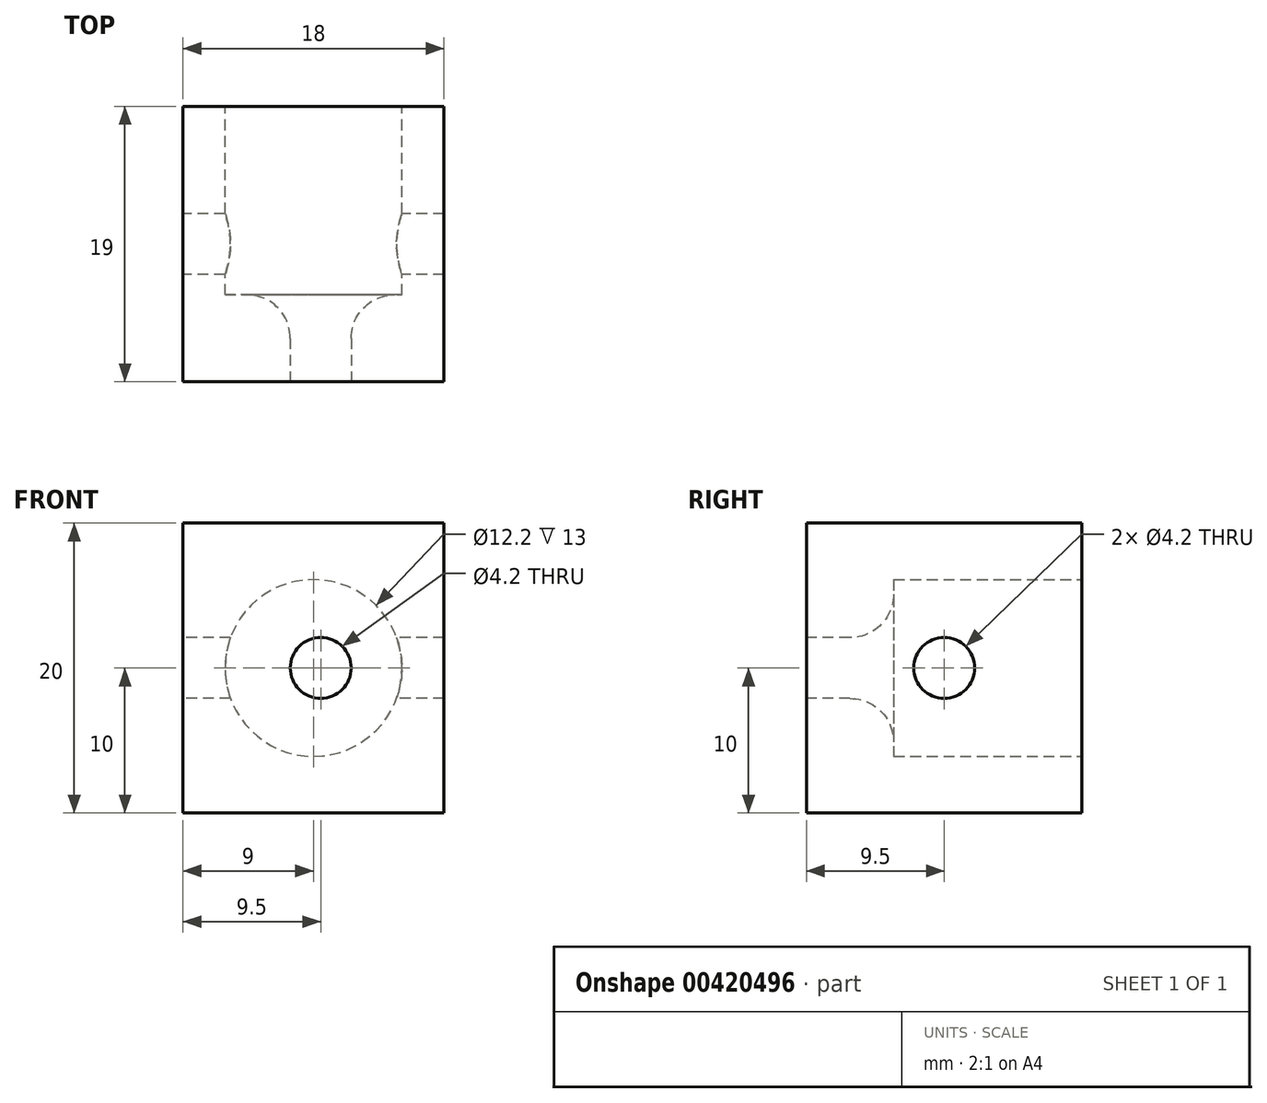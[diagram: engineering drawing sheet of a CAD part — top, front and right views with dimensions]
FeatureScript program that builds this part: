
annotation { "Feature Type Name" : "Feature", "Feature Type Description" : "" }
export const myFeature = defineFeature(function(context is Context, id is Id, definition is map)
    precondition{}
    {
        {
            var Q0;
            Q0=qCreatedBy(makeId("Top.planeOp"),FACE);
            var sketch = newSketch(context, id + "F0", { "sketchPlane" : qUnion([Q0])});
            skLineSegment(sketch, "E0.bottom", {"start": v(9, -9.5) * mm, "end": v(-9, -9.5) * mm});
            skLineSegment(sketch, "E0.top", {"start": v(9, 9.5) * mm, "end": v(-9, 9.5) * mm});
            skLineSegment(sketch, "E0.left", {"start": v(9, -9.5) * mm, "end": v(9, 9.5) * mm});
            skLineSegment(sketch, "E0.right", {"start": v(-9, -9.5) * mm, "end": v(-9, 9.5) * mm});
            skPoint(sketch, "E0.middle", {"position": v(0, 0) * mm});
            skSolve(sketch);
        }
        {
            var Q0;
            Q0=makeQuery(id+"F0.imprint","IMPRINT",FACE,{"disambiguationData":[TD([[makeQuery(id+"F0.imprint","IMPRINT",EDGE,{"derivedFrom":sQuery(id+"F0.wireOp",EDGE,"E0.bottom")}),-1.0]])]});
            extrude(context, id + "F1", {"entities" : qUnion([Q0]), "depth" : 20 * mm});
        }
        {
            var Q0;
            Q0=makeQuery(id+"F1.opExtrude","SWEPT_FACE",FACE,{"disambiguationData":[OSD([sQuery(id+"F0.wireOp",EDGE,"E0.bottom")])]});
            var sketch = newSketch(context, id + "F2", { "sketchPlane" : qUnion([Q0])});
            skLineSegment(sketch, "E1", {"start": v(-9, 10) * mm, "end": v(9, 10) * mm, "construction": true});
            skCircle(sketch, "E2", {"center": v(0.5, 10) * mm, "radius": 2.1 * mm});
            skSolve(sketch);
        }
        {
            var Q0;
            Q0=makeQuery(id+"F1.opExtrude","SWEPT_FACE",FACE,{"disambiguationData":[OSD([sQuery(id+"F0.wireOp",EDGE,"E0.top")])]});
            var sketch = newSketch(context, id + "F3", { "sketchPlane" : qUnion([Q0])});
            skLineSegment(sketch, "E3", {"start": v(-9, 10) * mm, "end": v(9, 10) * mm, "construction": true});
            skCircle(sketch, "E4", {"center": v(0, 10) * mm, "radius": 6.1 * mm});
            skSolve(sketch);
        }
        {
            var Q0;
            Q0=makeQuery(id+"F3.imprint","IMPRINT",FACE,{"disambiguationData":[TD([[makeQuery(id+"F3.imprint","IMPRINT",EDGE,{"derivedFrom":sQuery(id+"F3.wireOp",EDGE,"E4")}),1.0]])]});
            extrude(context, id + "F4", {"entities" : qUnion([Q0]), "operationType" : NewBodyOperationType.REMOVE, "oppositeDirection" : true, "depth" : 13 * mm});
        }
        {
            var Q0;
            Q0=makeQuery(id+"F2.imprint","IMPRINT",FACE,{"disambiguationData":[TD([[makeQuery(id+"F2.imprint","IMPRINT",EDGE,{"derivedFrom":sQuery(id+"F2.wireOp",EDGE,"E2")}),1.0]])]});
            extrude(context, id + "F5", {"entities" : qUnion([Q0]), "operationType" : NewBodyOperationType.REMOVE, "oppositeDirection" : true, "depth" : 18 * mm});
        }
        {
            var Q0;
            Q0=makeQuery(id+"F5.boolean.opBoolean","INTERSECT",EDGE,{"derivedFrom":[makeQuery(id+"F4.boolean.opBoolean","COPY",FACE,{"derivedFrom":makeQuery(id+"F4.opExtrude","CAP_FACE",FACE,{"disambiguationData":[OSD([sQuery(id+"F3.wireOp",EDGE,"E4")])],"isStart":false})}),makeQuery(id+"F5.opExtrude","SWEPT_FACE",FACE,{"disambiguationData":[OSD([sQuery(id+"F2.wireOp",EDGE,"E2")])]})]});
            fillet(context, id + "F6", {"entities" : qUnion([Q0]), "radius" : 3 * mm, "tangentPropagation" : true, "allowEdgeOverflow" : false});
        }
        {
            var Q0;
            Q0=makeQuery(id+"F1.opExtrude","SWEPT_FACE",FACE,{"disambiguationData":[OSD([sQuery(id+"F0.wireOp",EDGE,"E0.right")])]});
            var sketch = newSketch(context, id + "F7", { "sketchPlane" : qUnion([Q0])});
            skLineSegment(sketch, "E5", {"start": v(-9.5, 10) * mm, "end": v(9.5, 10) * mm, "construction": true});
            skCircle(sketch, "E6", {"center": v(0, 10) * mm, "radius": 2.1 * mm});
            skLineSegment(sketch, "E7", {"start": v(-9.5, 10) * mm, "end": v(9.5, 10) * mm});
            skSolve(sketch);
        }
        {
            var Q0;
            Q0=makeQuery(id+"F7.imprint","IMPRINT",FACE,{"disambiguationData":[TD([[makeQuery(id+"F7.imprint","IMPRINT",EDGE,{"derivedFrom":sQuery(id+"F7.wireOp",EDGE,"E6")}),1.0]])]});
            extrude(context, id + "F8", {"entities" : qUnion([Q0]), "operationType" : NewBodyOperationType.REMOVE, "oppositeDirection" : true, "depth" : 25 * mm});
        }
    });
